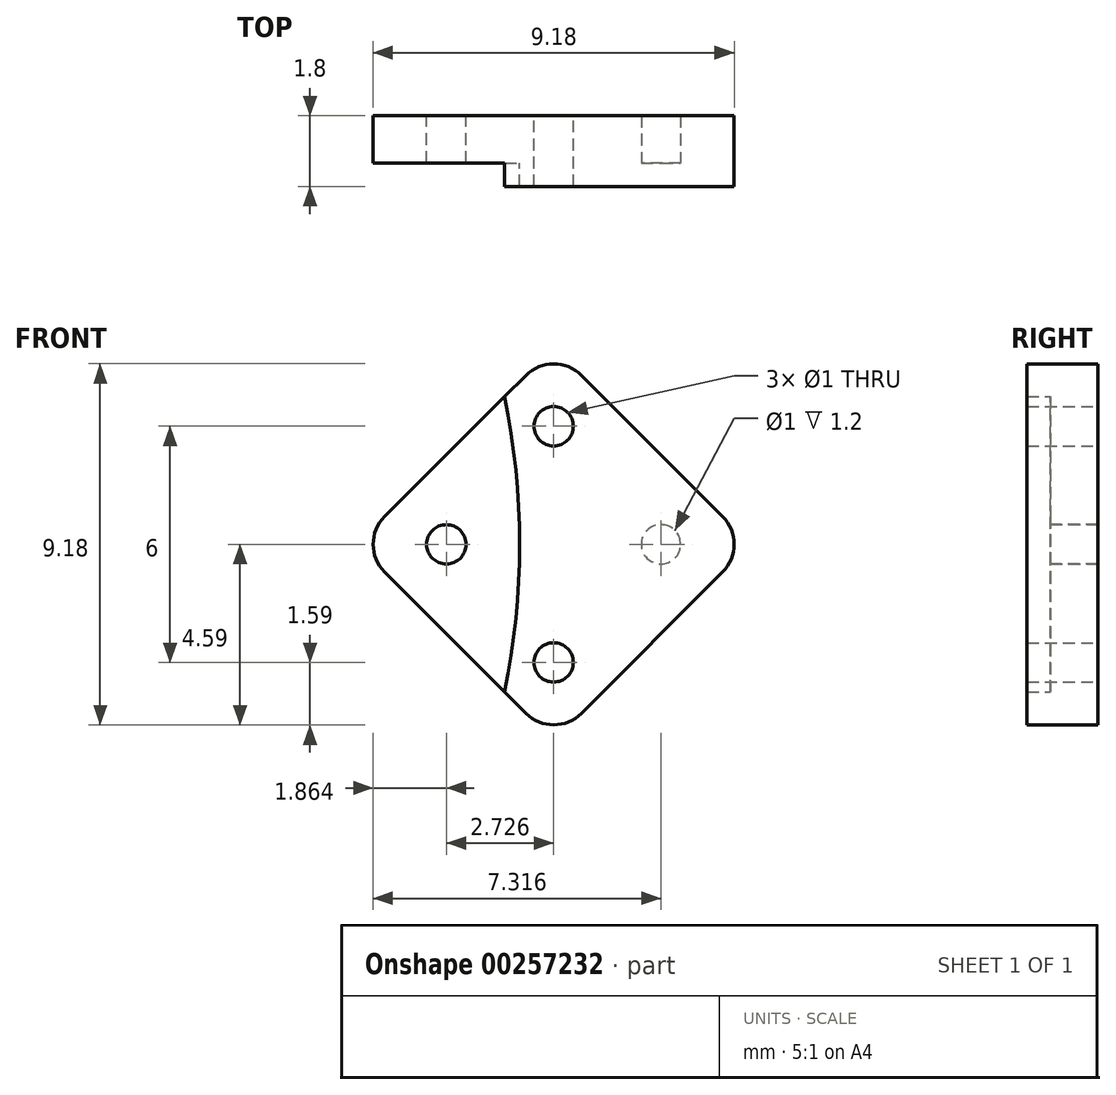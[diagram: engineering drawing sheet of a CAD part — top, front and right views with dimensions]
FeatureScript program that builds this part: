
annotation { "Feature Type Name" : "Feature", "Feature Type Description" : "" }
export const myFeature = defineFeature(function(context is Context, id is Id, definition is map)
    precondition{}
    {
        {
            var Q0;
            Q0=qCreatedBy(makeId("Front.planeOp"),FACE);
            var sketch = newSketch(context, id + "F0", { "sketchPlane" : qUnion([Q0])});
            skLineSegment(sketch, "E0", {"start": v(0, 5) * mm, "end": v(-5, 0) * mm});
            skLineSegment(sketch, "E1", {"start": v(-5, 0) * mm, "end": v(0, -5) * mm});
            skLineSegment(sketch, "E2", {"start": v(0, -5) * mm, "end": v(5, 0) * mm});
            skLineSegment(sketch, "E3", {"start": v(5, 0) * mm, "end": v(0, 5) * mm});
            skArc(sketch, "E4", {"start": v(0, -5) * mm, "mid": v(0.64, 0) * mm, "end": v(0, 5) * mm, "construction": true});
            skArc(sketch, "E5.0", {"start": v(-1.25, -3.75) * mm, "mid": v(-0.86, 0) * mm, "end": v(-1.25, 3.75) * mm});
            skSolve(sketch);
        }
        {
            var Q0;
            Q0=makeQuery(id+"F0.imprint","IMPRINT",FACE,{"disambiguationData":[TD([[makeQuery(id+"F0.imprint","IMPRINT",EDGE,{"derivedFrom":sQuery(id+"F0.wireOp",EDGE,"E2")}),1.0]])]});
            extrude(context, id + "F1", {"entities" : qUnion([Q0]), "depth" : 1.8 * mm});
        }
        {
            var Q0;
            Q0=makeQuery(id+"F0.imprint","IMPRINT",FACE,{"disambiguationData":[TD([[makeQuery(id+"F0.imprint","IMPRINT",EDGE,{"derivedFrom":sQuery(id+"F0.wireOp",EDGE,"E0")}),1.0]])]});
            extrude(context, id + "F2", {"entities" : qUnion([Q0]), "operationType" : NewBodyOperationType.ADD, "depth" : 1.2 * mm});
        }
        {
            var Q0;
            {var subQ1=sQuery(id+"F0.wireOp",EDGE,"E2");Q0=makeQuery(id+"F0.imprint","IMPRINT",FACE,{"disambiguationData":[TD([[makeQuery(id+"F0.imprint","IMPRINT",EDGE,{"derivedFrom":subQ1}),1.0]])]});}
            var sketch = newSketch(context, id + "F3", { "sketchPlane" : qUnion([Q0])});
            skPoint(sketch, "E6.0", {"position": v(0, 5) * mm});
            skPoint(sketch, "E7.0", {"position": v(0, -5) * mm});
            skLineSegment(sketch, "E8", {"start": v(0, 5) * mm, "end": v(0, -5) * mm, "construction": true});
            skArc(sketch, "E9.0", {"start": v(-1.25, -3.75) * mm, "mid": v(-0.86, 0) * mm, "end": v(-1.25, 3.75) * mm, "construction": true});
            skArc(sketch, "E10.MirrorCS", {"start": v(1.25, -3.75) * mm, "mid": v(0.86, 0) * mm, "end": v(1.25, 3.75) * mm});
            skLineSegment(sketch, "E11.0", {"start": v(5, 0) * mm, "end": v(1.25, 3.75) * mm});
            skLineSegment(sketch, "E12.0", {"start": v(1.25, -3.75) * mm, "end": v(5, 0) * mm});
            skSolve(sketch);
        }
        {
            var Q0;
            Q0=qSketchRegion(id+"F3",true);
            extrude(context, id + "F4", {"entities" : qUnion([Q0]), "operationType" : NewBodyOperationType.REMOVE, "depth" : 1.2 * mm});
        }
        {
            var Q0;
            Q0=makeQuery(id+"F1.opExtrude","SWEPT_EDGE",EDGE,{"disambiguationData":[OSD([sQuery(id+"F0.wireOp",EDGE,"E0"),sQuery(id+"F0.wireOp",EDGE,"E3")])]});
            var Q1;
            Q1=makeQuery(id+"F1.opExtrude","SWEPT_EDGE",EDGE,{"disambiguationData":[OSD([sQuery(id+"F0.wireOp",EDGE,"E2"),sQuery(id+"F0.wireOp",EDGE,"E3")])]});
            var Q2;
            Q2=makeQuery(id+"F1.opExtrude","SWEPT_EDGE",EDGE,{"disambiguationData":[OSD([sQuery(id+"F0.wireOp",EDGE,"E1"),sQuery(id+"F0.wireOp",EDGE,"E2")])]});
            var Q3;
            Q3=makeQuery(id+"F2.opExtrude","SWEPT_EDGE",EDGE,{"disambiguationData":[OSD([sQuery(id+"F0.wireOp",EDGE,"E0"),sQuery(id+"F0.wireOp",EDGE,"E1")])]});
            fillet(context, id + "F5", {"entities" : qUnion([Q0, Q1, Q2, Q3]), "radius" : 1 * mm, "tangentPropagation" : true, "allowEdgeOverflow" : false});
        }
        {
            var Q0;
            Q0=qCreatedBy(makeId("Front.planeOp"),FACE);
            var sketch = newSketch(context, id + "F6", { "sketchPlane" : qUnion([Q0])});
            skCircle(sketch, "E13", {"center": v(-2.73, 0) * mm, "radius": 0.5 * mm});
            skCircle(sketch, "E14", {"center": v(2.73, 0) * mm, "radius": 0.5 * mm});
            skCircle(sketch, "E15", {"center": v(0, 3) * mm, "radius": 0.5 * mm});
            skCircle(sketch, "E16", {"center": v(0, -3) * mm, "radius": 0.5 * mm});
            skSolve(sketch);
        }
        {
            var Q0;
            Q0=makeQuery(id+"F6.imprint","IMPRINT",FACE,{"disambiguationData":[TD([[makeQuery(id+"F6.imprint","IMPRINT",EDGE,{"derivedFrom":sQuery(id+"F6.wireOp",EDGE,"E13")}),1.0]])]});
            var Q1;
            Q1=makeQuery(id+"F6.imprint","IMPRINT",FACE,{"disambiguationData":[TD([[makeQuery(id+"F6.imprint","IMPRINT",EDGE,{"derivedFrom":sQuery(id+"F6.wireOp",EDGE,"E15")}),1.0]])]});
            var Q2;
            Q2=makeQuery(id+"F6.imprint","IMPRINT",FACE,{"disambiguationData":[TD([[makeQuery(id+"F6.imprint","IMPRINT",EDGE,{"derivedFrom":sQuery(id+"F6.wireOp",EDGE,"E16")}),1.0]])]});
            extrude(context, id + "F7", {"entities" : qUnion([Q0, Q1, Q2]), "operationType" : NewBodyOperationType.REMOVE, "endBound" : BoundingType.SYMMETRIC, "depth" : 25 * mm});
        }
        {
            var Q0;
            Q0=makeQuery(id+"F4.boolean.opBoolean","COPY",FACE,{"derivedFrom":makeQuery(id+"F4.opExtrude","CAP_FACE",FACE,{"disambiguationData":[OSD([sQuery(id+"F3.wireOp",EDGE,"E10.MirrorCS"),sQuery(id+"F3.wireOp",EDGE,"E11.0"),sQuery(id+"F3.wireOp",EDGE,"E12.0")])],"isStart":false})});
            var sketch = newSketch(context, id + "F8", { "sketchPlane" : qUnion([Q0])});
            skCircle(sketch, "E17.0", {"center": v(-2.73, 0) * mm, "radius": 0.5 * mm});
            skSolve(sketch);
        }
        {
            var Q0;
            Q0=makeQuery(id+"F8.imprint","IMPRINT",FACE,{"disambiguationData":[TD([[makeQuery(id+"F8.imprint","IMPRINT",EDGE,{"derivedFrom":sQuery(id+"F8.wireOp",EDGE,"E17.0")}),-1.0]])]});
            extrude(context, id + "F9", {"entities" : qUnion([Q0]), "operationType" : NewBodyOperationType.ADD, "depth" : 1.2 * mm});
        }
    });
